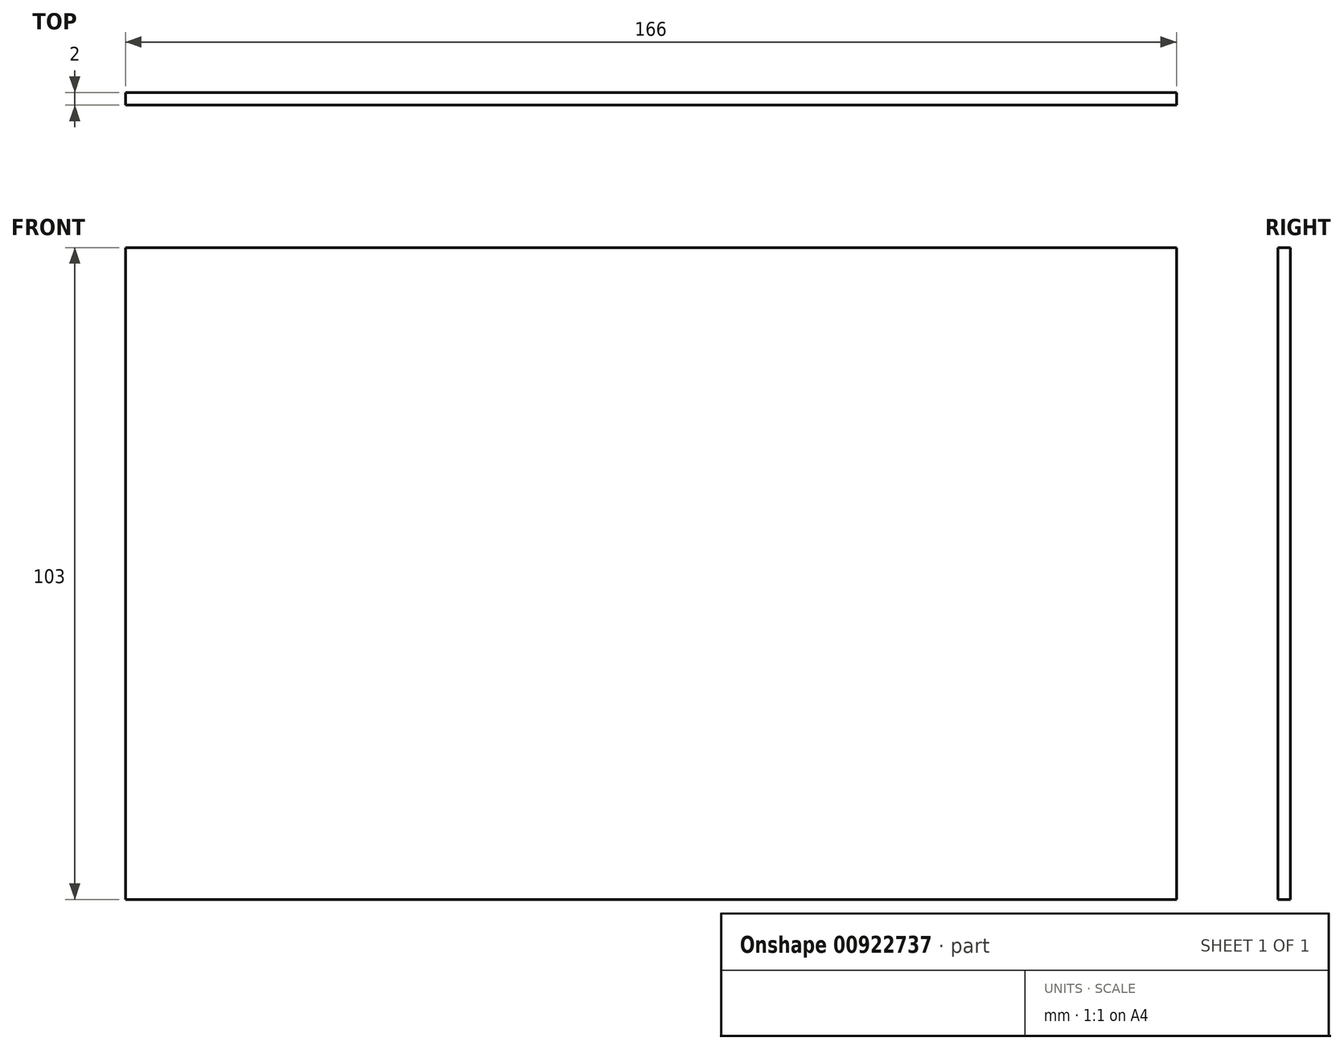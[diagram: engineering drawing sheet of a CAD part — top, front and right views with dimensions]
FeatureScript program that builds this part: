
annotation { "Feature Type Name" : "Feature", "Feature Type Description" : "" }
export const myFeature = defineFeature(function(context is Context, id is Id, definition is map)
    precondition{}
    {
        {
            var Q0;
            Q0=qCreatedBy(makeId("Front.planeOp"),FACE);
            var sketch = newSketch(context, id + "F0", { "sketchPlane" : qUnion([Q0])});
            skLineSegment(sketch, "E0.bottom", {"start": v(87, -51.5) * mm, "end": v(-87, -51.5) * mm});
            skLineSegment(sketch, "E0.top", {"start": v(87, 51.5) * mm, "end": v(-87, 51.5) * mm});
            skLineSegment(sketch, "E0.left", {"start": v(87, -51.5) * mm, "end": v(87, 51.5) * mm});
            skLineSegment(sketch, "E0.right", {"start": v(-87, -51.5) * mm, "end": v(-87, 51.5) * mm});
            skPoint(sketch, "E0.middle", {"position": v(0, 0) * mm});
            skLineSegment(sketch, "E1.bottom", {"start": v(-87, 51.5) * mm, "end": v(-83, 51.5) * mm});
            skLineSegment(sketch, "E1.top", {"start": v(-87, -51.5) * mm, "end": v(-83, -51.5) * mm});
            skLineSegment(sketch, "E1.left", {"start": v(-87, 51.5) * mm, "end": v(-87, -51.5) * mm});
            skLineSegment(sketch, "E1.right", {"start": v(-83, 51.5) * mm, "end": v(-83, -51.5) * mm});
            skLineSegment(sketch, "E2.bottom", {"start": v(87, 51.5) * mm, "end": v(83, 51.5) * mm});
            skLineSegment(sketch, "E2.top", {"start": v(87, -51.5) * mm, "end": v(83, -51.5) * mm});
            skLineSegment(sketch, "E2.left", {"start": v(87, 51.5) * mm, "end": v(87, -51.5) * mm});
            skLineSegment(sketch, "E2.right", {"start": v(83, 51.5) * mm, "end": v(83, -51.5) * mm});
            skLineSegment(sketch, "E3.bottom", {"start": v(-87, -51.5) * mm, "end": v(87, -51.5) * mm});
            skLineSegment(sketch, "E3.top", {"start": v(-87, -47.5) * mm, "end": v(87, -47.5) * mm});
            skLineSegment(sketch, "E3.left", {"start": v(-87, -51.5) * mm, "end": v(-87, -47.5) * mm});
            skLineSegment(sketch, "E3.right", {"start": v(87, -51.5) * mm, "end": v(87, -47.5) * mm});
            skSolve(sketch);
        }
        {
            var Q0;
            {var subQ0=sQuery(id+"F0.wireOp",EDGE,"E1.bottom");Q0=makeQuery(id+"F0.imprint","IMPRINT",FACE,{"disambiguationData":[TD([[makeQuery(id+"F0.imprint","IMPRINT",EDGE,{"derivedFrom":subQ0}),-1.0]])]});}
            var Q1;
            {var subQ5=sQuery(id+"F0.wireOp",EDGE,"E3.left");Q1=makeQuery(id+"F0.imprint","IMPRINT",FACE,{"disambiguationData":[TD([[makeQuery(id+"F0.imprint","IMPRINT",EDGE,{"derivedFrom":subQ5}),-1.0]])]});}
            var Q2;
            {var subQ0=sQuery(id+"F0.wireOp",EDGE,"E3.bottom");var subQ1=sQuery(id+"F0.wireOp",EDGE,"E1.right");var subQ2=makeQuery(id+"F0.imprint","INTERSECT",VERTEX,{"derivedFrom":[subQ1,subQ0]});Q2=makeQuery(id+"F0.imprint","IMPRINT",FACE,{"disambiguationData":[TD([[makeQuery(id+"F0.imprint","IMPRINT",EDGE,{"disambiguationData":[TD([[subQ2,1.0]])],"derivedFrom":subQ1}),1.0]])]});}
            var Q3;
            {var subQ0=sQuery(id+"F0.wireOp",EDGE,"E2.bottom");Q3=makeQuery(id+"F0.imprint","IMPRINT",FACE,{"disambiguationData":[TD([[makeQuery(id+"F0.imprint","IMPRINT",EDGE,{"derivedFrom":subQ0}),1.0]])]});}
            var Q4;
            {var subQ5=sQuery(id+"F0.wireOp",EDGE,"E3.right");Q4=makeQuery(id+"F0.imprint","IMPRINT",FACE,{"disambiguationData":[TD([[makeQuery(id+"F0.imprint","IMPRINT",EDGE,{"derivedFrom":subQ5}),1.0]])]});}
            extrude(context, id + "F1", {"entities" : qUnion([Q0, Q1, Q2, Q3, Q4]), "endBound" : BoundingType.SYMMETRIC, "depth" : 2 * mm, "offsetDistance" : 25 * mm});
        }
    });
